# Revit family: Maxi Rack
name_source: partatom
category: Furniture
units: mm (PartAtom-declared; Revit-internal decimal feet)

## family parameters
Always vertical = Yes
Cut with Voids When Loaded = No
OmniClass Number = 23.40.20.00
OmniClass Title = General Furniture and Specialties
Room Calculation Point = No
Shared = No
Work Plane-Based = No

## types (78) — shared parameters

## per-type parameters (varying)
| type | Unit Depth | Unit Width |
| 18" D 24" W | 1' - 6" | 2' - 0" |
| 18" D 30" W | 1' - 6" | 2' - 6" |
| 18" D 36" W | 1' - 6" | 3' - 0" |
| 18" D 42" W | 1' - 6" | 3' - 6" |
| 18" D 48" W | 1' - 6" | 4' - 0" |
| 18" D 54" W | 1' - 6" | 4' - 6" |
| 18" D 60" W | 1' - 6" | 5' - 0" |
| 18" D 66" W | 1' - 6" | 5' - 6" |
| 18" D 72" W | 1' - 6" | 6' - 0" |
| 18" D 78" W | 1' - 6" | 6' - 6" |
| 18" D 84" W | 1' - 6" | 7' - 0" |
| 18" D 90" W | 1' - 6" | 7' - 6" |
| 18" D 96" W | 1' - 6" | 8' - 0" |
| 24" D 24" W | 2' - 0" | 2' - 0" |
| 24" D 30" W | 2' - 0" | 2' - 6" |
| 24" D 36"W | 2' - 0" | 3' - 0" |
| 24" D 42" W | 2' - 0" | 3' - 6" |
| 24" D 48" W | 2' - 0" | 4' - 0" |
| 24" D 54" W | 2' - 0" | 4' - 6" |
| 24" D 60" W | 2' - 0" | 5' - 0" |
| 24" D 72" W | 2' - 0" | 6' - 0" |
| 24" D 66" W | 2' - 0" | 5' - 6" |
| 24" D 78" W | 2' - 0" | 6' - 6" |
| 24" D 84" W | 2' - 0" | 7' - 0" |
| 24" D 90" W | 2' - 0" | 7' - 6" |
| 24" D 96" W | 2' - 0" | 8' - 0" |
| 30" D 24" W | 2' - 6" | 2' - 0" |
| 30" D 30" W | 2' - 6" | 2' - 6" |
| 30" D 36" W | 2' - 6" | 3' - 0" |
| 30" D 42" W | 2' - 6" | 3' - 6" |
| 30" D 48" W | 2' - 6" | 4' - 0" |
| 30" D 54" W | 2' - 6" | 4' - 6" |
| 30" D 60" W | 2' - 6" | 5' - 0" |
| 30" D 66" W | 2' - 6" | 5' - 6" |
| 30" D 72" W | 2' - 6" | 6' - 0" |
| 30" D 78" W | 2' - 6" | 6' - 6" |
| 30" D 84" W | 2' - 6" | 7' - 0" |
| 30" D 96" W | 2' - 6" | 8' - 0" |
| 30" D 90" W | 2' - 6" | 7' - 6" |
| 36" D 24" W | 3' - 0" | 2' - 0" |
| 36" D 30" W | 3' - 0" | 2' - 6" |
| 36" D 36" W | 3' - 0" | 3' - 0" |
| 36" D 42" W | 3' - 0" | 3' - 6" |
| 36" D 48" W | 3' - 0" | 4' - 0" |
| 36" D 54" W | 3' - 0" | 4' - 6" |
| 36" D 60" W | 3' - 0" | 5' - 0" |
| 36" D 66" W | 3' - 0" | 5' - 6" |
| 36" D 72" W | 3' - 0" | 6' - 0" |
| 36" D 78" W | 3' - 0" | 6' - 6" |
| 36" D 84" W | 3' - 0" | 7' - 0" |
| 36" D 90" W | 3' - 0" | 7' - 6" |
| 36" D 96" W | 3' - 0" | 8' - 0" |
| 42" D 24" W | 3' - 6" | 2' - 0" |
| 42" D 30" W | 3' - 6" | 2' - 6" |
| 42" D 36" W | 3' - 6" | 3' - 0" |
| 42" D 42" W | 3' - 6" | 3' - 6" |
| 42" D 48" W | 3' - 6" | 4' - 0" |
| 42" D 54" W | 3' - 6" | 4' - 6" |
| 42" D 60" W | 3' - 6" | 5' - 0" |
| 42" D 66" W | 3' - 6" | 5' - 6" |
| 42" D 72" W | 3' - 6" | 6' - 0" |
| 42" D 78" W | 3' - 6" | 6' - 6" |
| 42" D 84" W | 3' - 6" | 7' - 0" |
| 42" D 90" W | 3' - 6" | 7' - 6" |
| 42" D 96" W | 3' - 6" | 8' - 0" |
| 48" D 24" W | 4' - 0" | 2' - 0" |
| 48" D 30" W | 4' - 0" | 2' - 6" |
| 48" D 36" W | 4' - 0" | 3' - 0" |
| 48" D 42" W | 4' - 0" | 3' - 6" |
| 48" D 48" W | 4' - 0" | 4' - 0" |
| 48" D 54" W | 4' - 0" | 4' - 6" |
| 48" D 60" W | 4' - 0" | 5' - 0" |
| 48" D 66" W | 4' - 0" | 5' - 6" |
| 48" D 72" W | 4' - 0" | 6' - 0" |
| 48" D 78" W | 4' - 0" | 6' - 6" |
| 48" D 84" W | 4' - 0" | 7' - 0" |
| 48" D 90" W | 4' - 0" | 7' - 6" |
| 48" D 96" W | 4' - 0" | 8' - 0" |

## geometry (parser evidence)
native form markers: Sweep x45
no freeform markers — native parametric forms only
